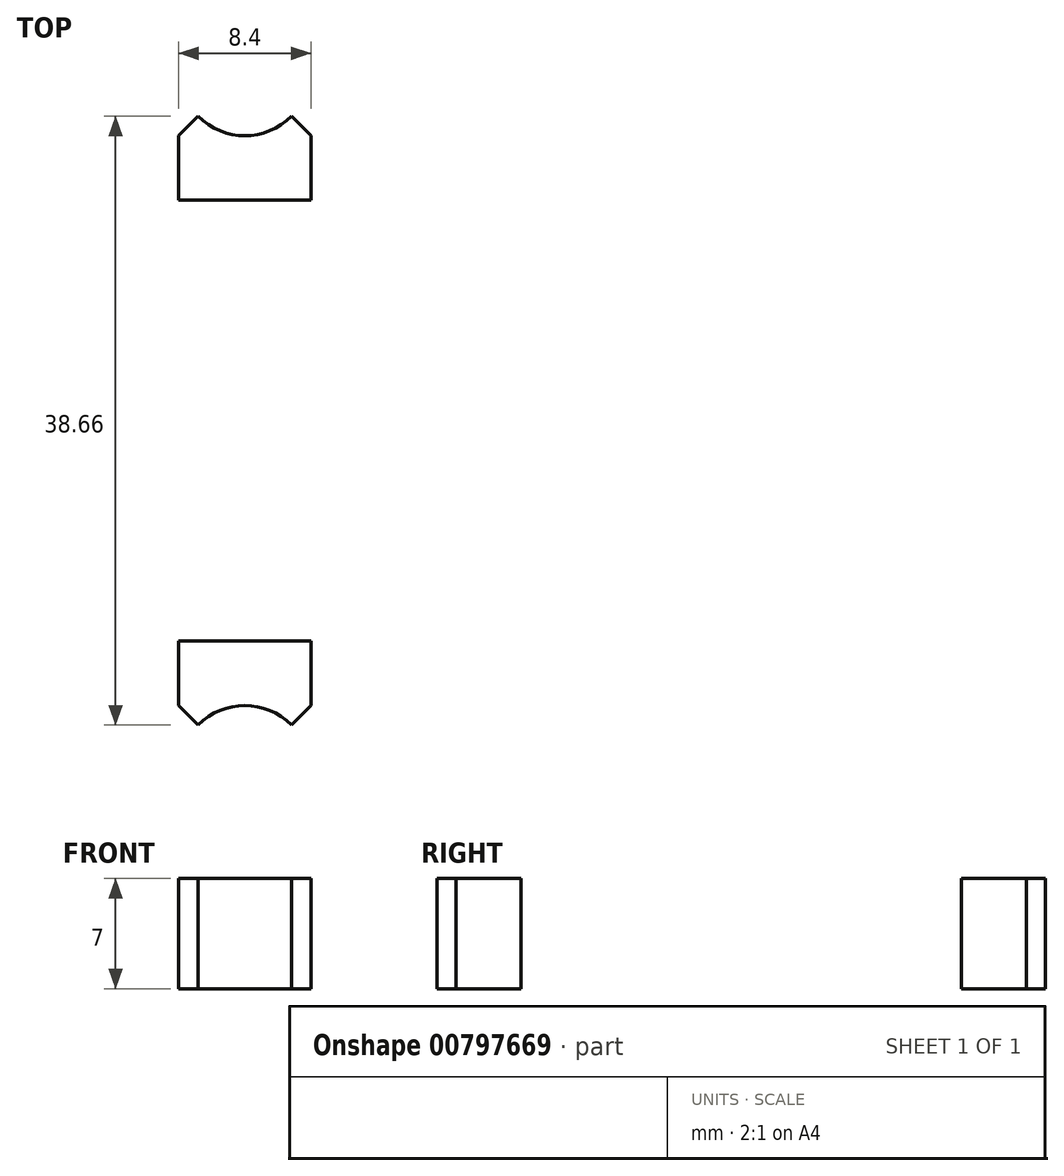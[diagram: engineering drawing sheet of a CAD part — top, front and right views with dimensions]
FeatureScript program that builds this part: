
annotation { "Feature Type Name" : "Feature", "Feature Type Description" : "" }
export const myFeature = defineFeature(function(context is Context, id is Id, definition is map)
    precondition{}
    {
        {
            var Q0;
            Q0=qCreatedBy(makeId("Top.planeOp"),FACE);
            var sketch = newSketch(context, id + "F0", { "sketchPlane" : qUnion([Q0])});
            skLineSegment(sketch, "E0.bottom", {"start": v(4.2, 26.5) * mm, "end": v(-4.2, 26.5) * mm});
            skLineSegment(sketch, "E0.top", {"start": v(4.2, -26.5) * mm, "end": v(-4.2, -26.5) * mm});
            skLineSegment(sketch, "E0.left", {"start": v(4.2, 26.5) * mm, "end": v(4.2, -26.5) * mm});
            skLineSegment(sketch, "E0.right", {"start": v(-4.2, 26.5) * mm, "end": v(-4.2, -26.5) * mm});
            skPoint(sketch, "E0.middle", {"position": v(0, 0) * mm});
            skCircle(sketch, "E1", {"center": v(0, -22.3) * mm, "radius": 4.2 * mm});
            skPoint(sketch, "E1.first.point", {"position": v(4, -21) * mm});
            skPoint(sketch, "E1.second.point", {"position": v(-3.93, -20.8) * mm});
            skPoint(sketch, "E1.third.point", {"position": v(0, -26.5) * mm});
            skCircle(sketch, "E2", {"center": v(0, 22.3) * mm, "radius": 4.2 * mm});
            skPoint(sketch, "E2.first.point", {"position": v(-3.27, 19.67) * mm});
            skPoint(sketch, "E2.second.point", {"position": v(3.6, 20.12) * mm});
            skPoint(sketch, "E2.third.point", {"position": v(0, 26.5) * mm});
            skLineSegment(sketch, "E3.left", {"start": v(4.2, 0) * mm, "end": v(4.2, 0) * mm});
            skLineSegment(sketch, "E3.right", {"start": v(-4.2, 0) * mm, "end": v(-4.2, 0) * mm});
            skLineSegment(sketch, "E4", {"start": v(0, -22.3) * mm, "end": v(4.2, -22.3) * mm});
            skLineSegment(sketch, "E5", {"start": v(0, -22.3) * mm, "end": v(4.2, -18.1) * mm});
            skLineSegment(sketch, "E6", {"start": v(0, 0) * mm, "end": v(0, -26.5) * mm});
            skLineSegment(sketch, "E7", {"start": v(0, 0) * mm, "end": v(4.2, 0) * mm});
            skLineSegment(sketch, "E8.MirrorCS", {"start": v(0, -22.3) * mm, "end": v(-4.2, -18.1) * mm});
            skLineSegment(sketch, "E9.MirrorCS", {"start": v(0, 22.3) * mm, "end": v(4.2, 18.1) * mm});
            skLineSegment(sketch, "E10.MirrorCS", {"start": v(0, 22.3) * mm, "end": v(-4.2, 18.1) * mm});
            skLineSegment(sketch, "E11.bottom", {"start": v(4.2, -14) * mm, "end": v(-4.2, -14) * mm});
            skLineSegment(sketch, "E11.top", {"start": v(4.2, 14) * mm, "end": v(-4.2, 14) * mm});
            skLineSegment(sketch, "E11.left", {"start": v(4.2, -14) * mm, "end": v(4.2, 14) * mm});
            skLineSegment(sketch, "E11.right", {"start": v(-4.2, -14) * mm, "end": v(-4.2, 14) * mm});
            skSolve(sketch);
        }
        {
            var Q0;
            {var subQ0=sQuery(id+"F0.wireOp",EDGE,"E3.bottom");Q0=makeQuery(id+"F0.imprint","IMPRINT",FACE,{"disambiguationData":[TD([[makeQuery(id+"F0.imprint","IMPRINT",EDGE,{"derivedFrom":subQ0}),-1.0]])]});}
            var Q1;
            {var subQ0=sQuery(id+"F0.wireOp",EDGE,"E3.top");Q1=makeQuery(id+"F0.imprint","IMPRINT",FACE,{"disambiguationData":[TD([[makeQuery(id+"F0.imprint","IMPRINT",EDGE,{"derivedFrom":subQ0}),1.0]])]});}
            var Q2;
            {var subQ1=sQuery(id+"F0.wireOp",EDGE,"E1");var subQ5=sQuery(id+"F0.wireOp",EDGE,"E5");var subQ8=makeQuery(id+"F0.imprint","INTERSECT",VERTEX,{"derivedFrom":[subQ1,subQ5]});Q2=makeQuery(id+"F0.imprint","IMPRINT",FACE,{"disambiguationData":[TD([[makeQuery(id+"F0.imprint","IMPRINT",EDGE,{"disambiguationData":[TD([[subQ8,-1.0]])],"derivedFrom":subQ1}),-1.0]])]});}
            var Q3;
            {var subQ3=sQuery(id+"F0.wireOp",EDGE,"E1");var subQ5=sQuery(id+"F0.wireOp",EDGE,"E6");var subQ6=makeQuery(id+"F0.imprint","INTERSECT",VERTEX,{"derivedFrom":[subQ3,subQ5]});Q3=makeQuery(id+"F0.imprint","IMPRINT",FACE,{"disambiguationData":[TD([[makeQuery(id+"F0.imprint","IMPRINT",EDGE,{"disambiguationData":[TD([[subQ6,-1.0]])],"derivedFrom":subQ3}),-1.0]])]});}
            var Q4;
            {var subQ9=sQuery(id+"F0.wireOp",EDGE,"E11.top");Q4=makeQuery(id+"F0.imprint","IMPRINT",FACE,{"disambiguationData":[TD([[makeQuery(id+"F0.imprint","IMPRINT",EDGE,{"derivedFrom":subQ9}),-1.0]])]});}
            extrude(context, id + "F1", {"entities" : qUnion([Q0, Q1, Q2, Q3, Q4]), "depth" : 7 * mm, "offsetDistance" : 25 * mm});
        }
    });
